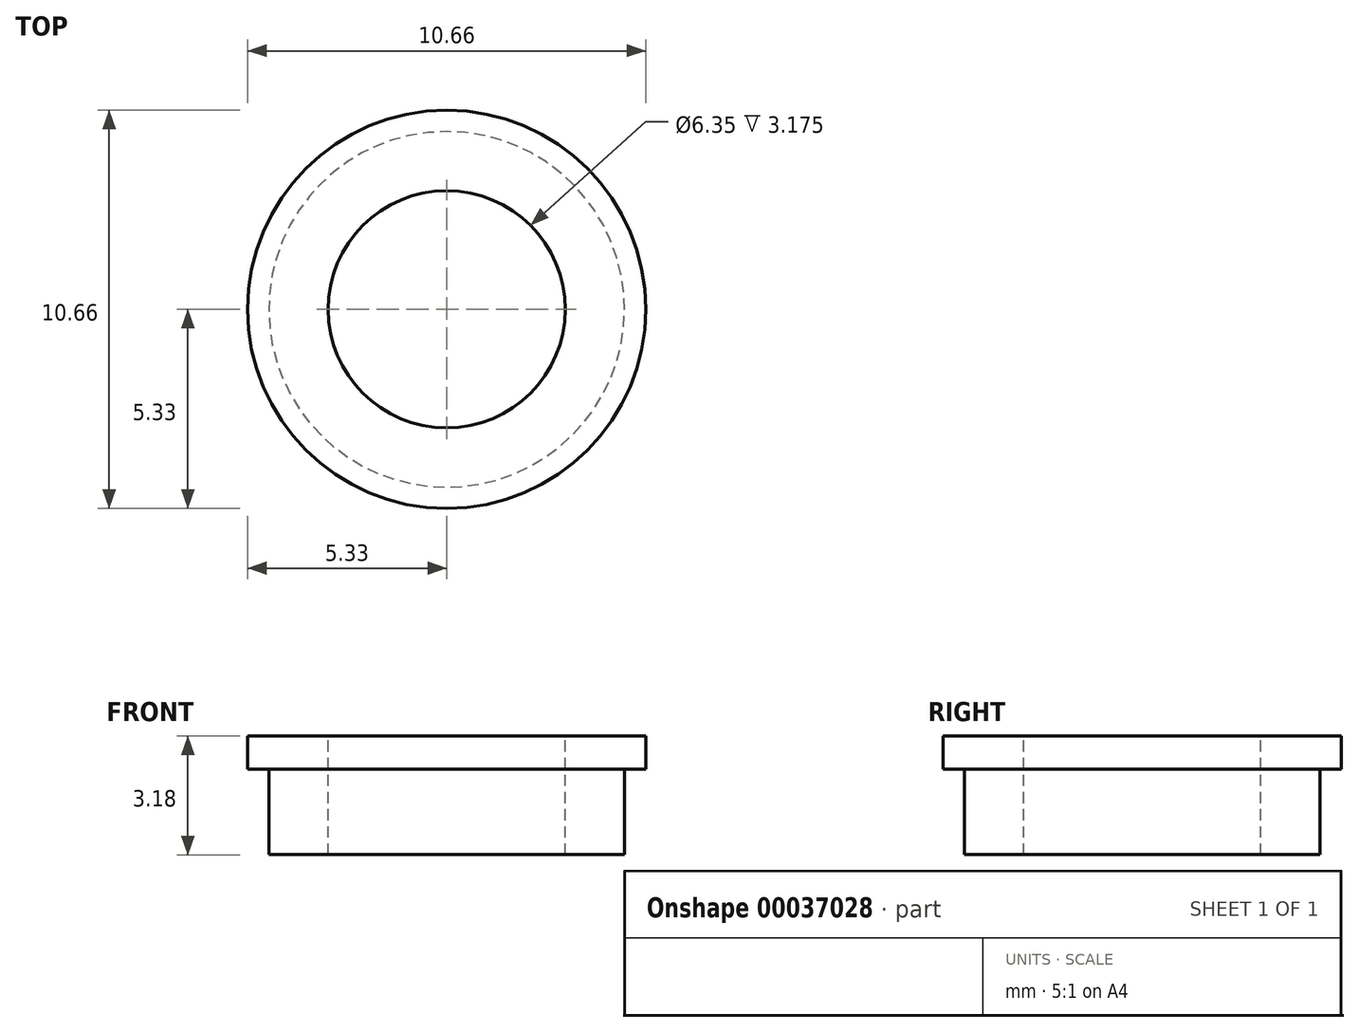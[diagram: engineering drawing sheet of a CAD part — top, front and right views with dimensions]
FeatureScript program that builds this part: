
annotation { "Feature Type Name" : "Feature", "Feature Type Description" : "" }
export const myFeature = defineFeature(function(context is Context, id is Id, definition is map)
    precondition{}
    {
        {
            var Q0;
            Q0=qCreatedBy(makeId("Front.planeOp"),FACE);
            var sketch = newSketch(context, id + "F0", { "sketchPlane" : qUnion([Q0])});
            skLineSegment(sketch, "E0", {"start": v(0, 1.59) * mm, "end": v(0, -1.59) * mm, "construction": true});
            skLineSegment(sketch, "E1", {"start": v(3.18, -1.59) * mm, "end": v(3.18, 1.59) * mm});
            skLineSegment(sketch, "E2", {"start": v(3.18, 1.59) * mm, "end": v(5.33, 1.59) * mm});
            skLineSegment(sketch, "E3", {"start": v(5.33, 1.59) * mm, "end": v(5.33, 0.7) * mm});
            skLineSegment(sketch, "E4", {"start": v(5.33, 0.7) * mm, "end": v(4.76, 0.7) * mm});
            skLineSegment(sketch, "E5", {"start": v(4.76, 0.7) * mm, "end": v(4.76, -1.59) * mm});
            skLineSegment(sketch, "E6", {"start": v(4.76, -1.59) * mm, "end": v(3.18, -1.59) * mm});
            skLineSegment(sketch, "E7", {"start": v(0, 1.59) * mm, "end": v(3.18, 1.59) * mm, "construction": true});
            skLineSegment(sketch, "E8", {"start": v(0, -1.59) * mm, "end": v(3.18, -1.59) * mm, "construction": true});
            skSolve(sketch);
        }
        {
            var Q0;
            Q0 = qSketchRegion(id + "F0", true);
            var Q1;
            Q1=sQuery(id+"F0.wireOp",EDGE,"E0");
            revolve(context, id + "F1", {"entities" : qUnion([Q0]), "axis" : qUnion([Q1]), "revolveType" : RevolveType.FULL});
        }
    });
